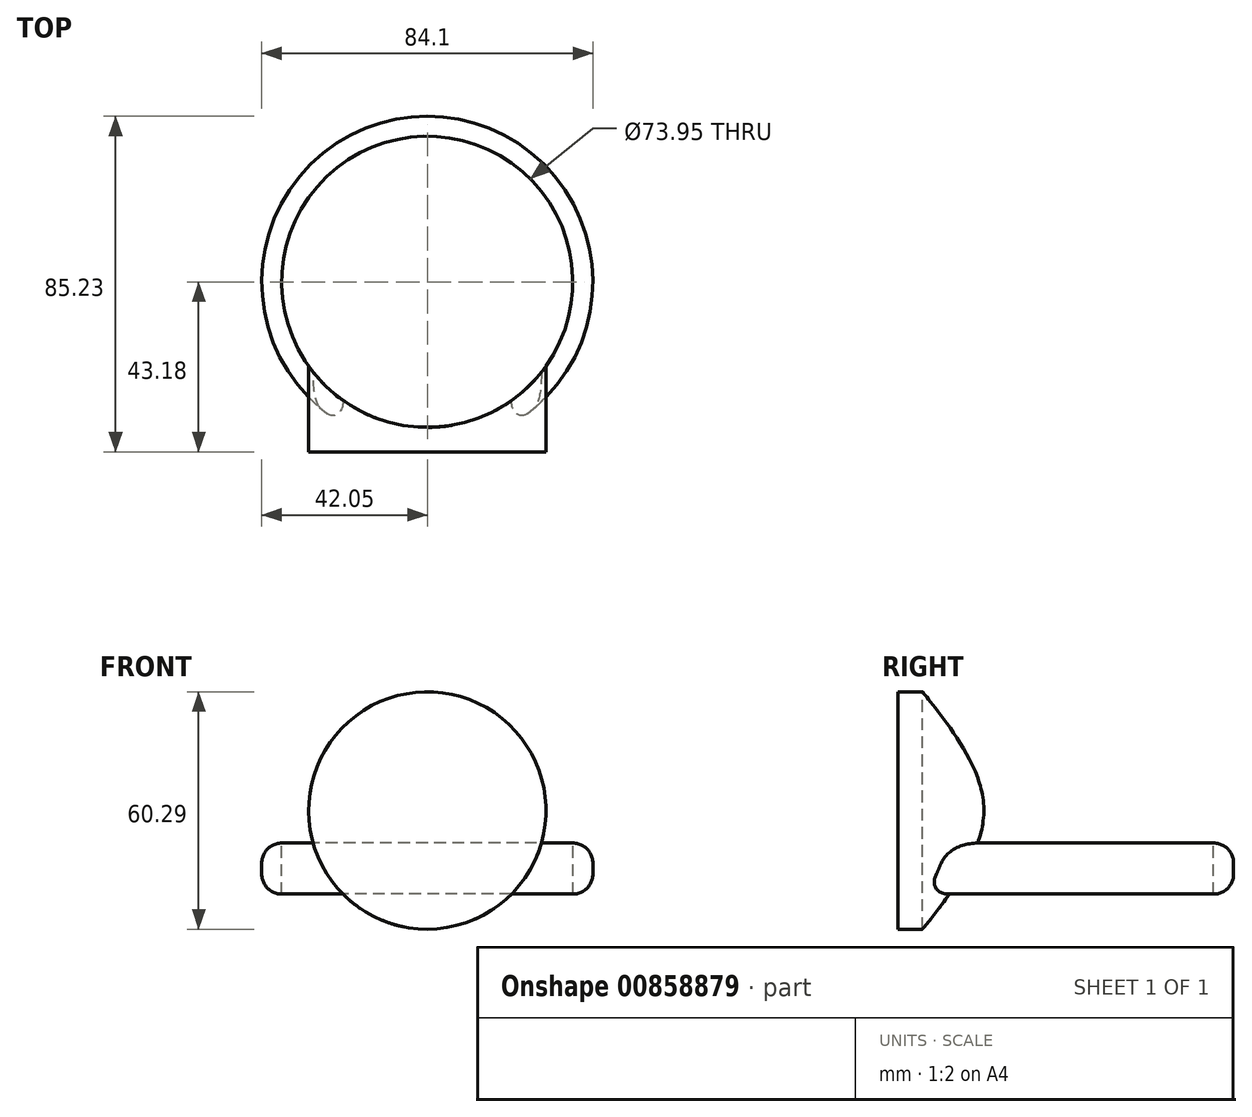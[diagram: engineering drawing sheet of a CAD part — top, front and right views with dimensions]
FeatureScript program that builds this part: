
annotation { "Feature Type Name" : "Feature", "Feature Type Description" : "" }
export const myFeature = defineFeature(function(context is Context, id is Id, definition is map)
    precondition{}
    {
        {
            var Q0;
            Q0=qCreatedBy(makeId("Top.planeOp"),FACE);
            var sketch = newSketch(context, id + "F0", { "sketchPlane" : qUnion([Q0])});
            skCircle(sketch, "E0", {"center": v(0, 0) * mm, "radius": 42.05 * mm});
            skSolve(sketch);
        }
        {
            var Q0;
            Q0=makeQuery(id+"F0.imprint","IMPRINT",FACE,{"disambiguationData":[TD([[makeQuery(id+"F0.imprint","IMPRINT",EDGE,{"derivedFrom":sQuery(id+"F0.wireOp",EDGE,"E0")}),1.0]])]});
            extrude(context, id + "F1", {"entities" : qUnion([Q0]), "depth" : 12.95 * mm, "offsetDistance" : 25.4 * mm});
        }
        {
            var Q0;
            Q0=makeQuery(id+"F1.opExtrude","CAP_EDGE",EDGE,{"disambiguationData":[OSD([sQuery(id+"F0.wireOp",EDGE,"E0")])],"isStart":false});
            var Q1;
            Q1=makeQuery(id+"F1.opExtrude","CAP_EDGE",EDGE,{"disambiguationData":[OSD([sQuery(id+"F0.wireOp",EDGE,"E0")])],"isStart":true});
            fillet(context, id + "F2", {"entities" : qUnion([Q0, Q1]), "radius" : 5.08 * mm, "tangentPropagation" : true, "allowEdgeOverflow" : false});
        }
        {
            var Q0;
            Q0=makeQuery(id+"F1.opExtrude","CAP_FACE",FACE,{"disambiguationData":[OSD([sQuery(id+"F0.wireOp",EDGE,"E0")])],"isStart":false});
            extrude(context, id + "F3", {"entities" : qUnion([Q0]), "operationType" : NewBodyOperationType.REMOVE, "oppositeDirection" : true, "depth" : 41.15 * mm, "offsetDistance" : 25.4 * mm});
        }
        {
            var Q0;
            Q0=qCreatedBy(makeId("Front.planeOp"),FACE);
            var sketch = newSketch(context, id + "F4", { "sketchPlane" : qUnion([Q0])});
            skCircle(sketch, "E1", {"center": v(0, 21.22) * mm, "radius": 30.15 * mm});
            skSolve(sketch);
        }
        {
            var Q0;
            Q0=makeQuery(id+"F4.imprint","IMPRINT",FACE,{"disambiguationData":[TD([[makeQuery(id+"F4.imprint","IMPRINT",EDGE,{"derivedFrom":sQuery(id+"F4.wireOp",EDGE,"E1")}),1.0]])]});
            extrude(context, id + "F5", {"entities" : qUnion([Q0]), "operationType" : NewBodyOperationType.ADD, "depth" : 43.18 * mm, "offsetDistance" : 25.4 * mm});
        }
        {
            var Q0;
            Q0=qCreatedBy(makeId("Top.planeOp"),FACE);
            var sketch = newSketch(context, id + "F6", { "sketchPlane" : qUnion([Q0])});
            skCircle(sketch, "E2", {"center": v(0, 0) * mm, "radius": 36.97 * mm});
            skSolve(sketch);
        }
        {
            var Q0;
            Q0=makeQuery(id+"F6.imprint","IMPRINT",FACE,{"disambiguationData":[TD([[makeQuery(id+"F6.imprint","IMPRINT",EDGE,{"derivedFrom":sQuery(id+"F6.wireOp",EDGE,"E2")}),1.0]])]});
            extrude(context, id + "F7", {"entities" : qUnion([Q0]), "operationType" : NewBodyOperationType.REMOVE, "depth" : 77.47 * mm, "offsetDistance" : 25.4 * mm});
        }
        {
            var Q0;
            Q0=qCreatedBy(makeId("Top.planeOp"),FACE);
            var sketch = newSketch(context, id + "F8", { "sketchPlane" : qUnion([Q0])});
            skCircle(sketch, "E3", {"center": v(0, 0) * mm, "radius": 36.97 * mm});
            skSolve(sketch);
        }
        {
            var Q0;
            Q0=makeQuery(id+"F8.imprint","IMPRINT",FACE,{"disambiguationData":[TD([[makeQuery(id+"F8.imprint","IMPRINT",EDGE,{"derivedFrom":sQuery(id+"F8.wireOp",EDGE,"E3")}),1.0]])]});
            extrude(context, id + "F9", {"entities" : qUnion([Q0]), "operationType" : NewBodyOperationType.REMOVE, "oppositeDirection" : true, "depth" : 29.46 * mm, "offsetDistance" : 25.4 * mm});
        }
    });
